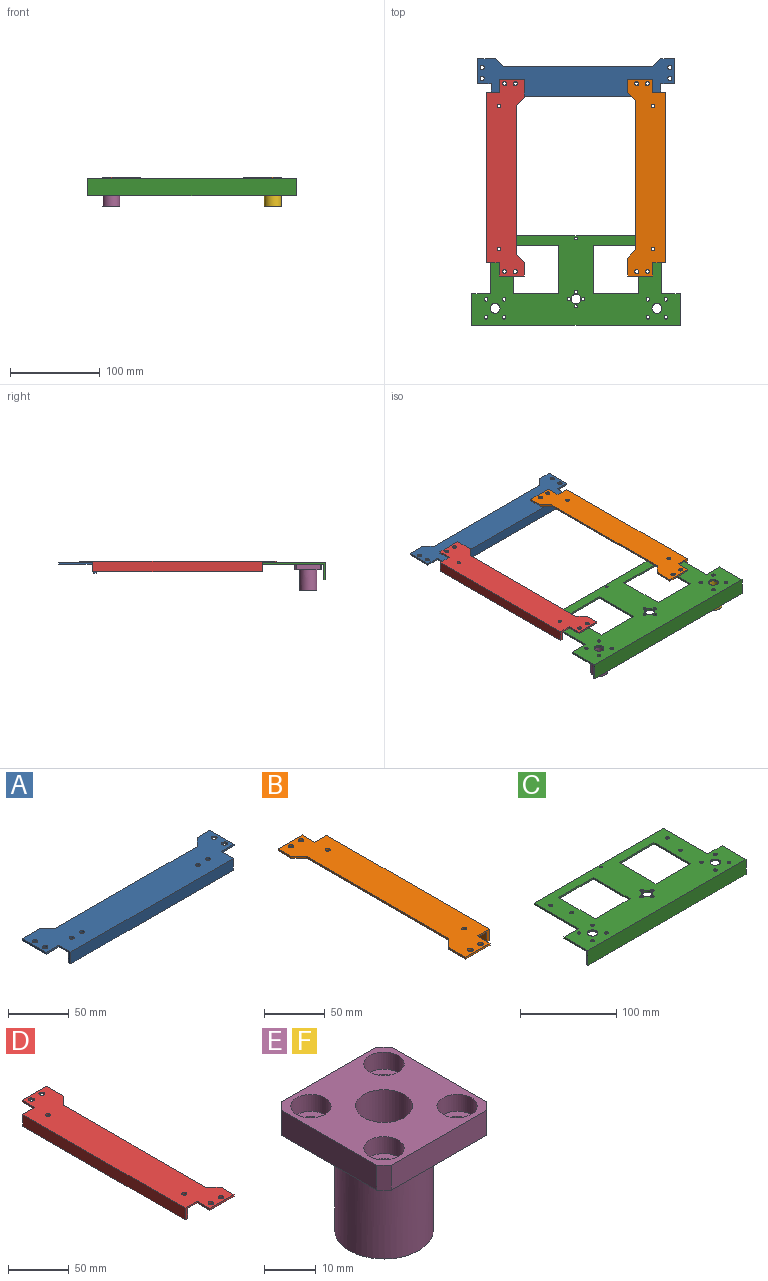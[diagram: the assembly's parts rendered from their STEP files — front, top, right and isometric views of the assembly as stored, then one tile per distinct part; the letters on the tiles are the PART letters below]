
ASSEMBLY  parts=6 mates=5
PART A: 24 faces, bbox 219x42x11.8 mm
  f0: plane 219x39mm, normal (0,0,-1), area 6519.3mm2, adj f2,f3,f4,f5,f6,f7,f8,f9
  f1: plane 219x42mm, normal (0,0,1), area 7086.3mm2, adj f2,f3,f4,f5,f6,f7,f8,f9
  f2: plane 14x11.8mm, normal (1,0,0), area 55.2mm2, adj f0,f1,f3,f18,f20,f21
  f3: plane 15x1.8mm, normal (0,-1,0), area 27mm2, adj f0,f1,f2,f4
  f4: plane 28x1.8mm, normal (1,0,0), area 50.4mm2, adj f0,f1,f3,f5
  f5: plane 15x1.8mm, normal (0,1,0), area 27mm2, adj f0,f1,f4,f6
  f6: plane 9x9mm, normal (-0.71,0.71,0), area 22.9mm2, adj f0,f1,f5,f7
  f7: plane 166x1.8mm, normal (0,1,0), area 298.8mm2, adj f0,f1,f6,f8
  f8: plane 9x9mm, normal (0.71,0.71,0), area 22.9mm2, adj f0,f1,f7,f9
  f9: plane 20x1.8mm, normal (0,1,0), area 36mm2, adj f0,f1,f8,f10
  f10: plane 28x1.8mm, normal (-1,0,0), area 50.4mm2, adj f0,f1,f9,f11
  f11: plane 15x1.8mm, normal (0,-1,0), area 27mm2, adj f0,f1,f10,f12
  f12: plane 14x11.8mm, normal (-1,0,0), area 55.2mm2, adj f0,f1,f11,f18,f20,f21
  f13: cylinder r=2.3mm len=4.6mm, axis (0,0,-1), area 26mm2, adj f0,f1
  f14: cylinder r=2.3mm len=4.6mm, axis (0,0,-1), area 26mm2, adj f0,f1
  f15: cylinder r=2.3mm len=4.6mm, axis (0,0,-1), area 26mm2, adj f0,f1
  f16: cylinder r=2.3mm len=4.6mm, axis (0,0,-1), area 26mm2, adj f0,f1
  f17: cylinder r=2mm len=4mm, axis (0,0,-1), area 22.6mm2, adj f0,f1
  f18: plane 189x11.8mm, normal (0,-1,0), area 2230.2mm2, adj f1,f2,f12,f21
  f19: cylinder r=2mm len=4mm, axis (0,0,-1), area 22.6mm2, adj f0,f1
  f20: plane 189x10mm, normal (0,1,0), area 1890mm2, adj f0,f2,f12,f21
  f21: plane 189x3mm, normal (0,0,-1), area 567mm2, adj f2,f12,f18,f20
  f22: cylinder r=2mm len=4mm, axis (0,0,-1), area 22.6mm2, adj f0,f1
  f23: cylinder r=2mm len=4mm, axis (0,0,-1), area 22.6mm2, adj f0,f1
PART B: 22 faces, bbox 42x219x11.8 mm
  f0: plane 219x39mm, normal (0,0,-1), area 6544.4mm2, adj f1,f2,f3,f4,f5,f6,f7,f8
  f1: plane 14x11.8mm, normal (0,1,0), area 55.2mm2, adj f0,f2,f17,f19,f20,f21
  f2: plane 15x1.8mm, normal (1,0,0), area 27mm2, adj f0,f1,f3,f19
  f3: plane 28x1.8mm, normal (0,1,0), area 50.4mm2, adj f0,f2,f4,f19
  f4: plane 15x1.8mm, normal (-1,0,0), area 27mm2, adj f0,f3,f5,f19
  f5: plane 9x9mm, normal (-0.71,-0.71,0), area 22.9mm2, adj f0,f4,f6,f19
  f6: plane 166x1.8mm, normal (-1,0,0), area 298.8mm2, adj f0,f5,f7,f19
  f7: plane 9x9mm, normal (-0.71,0.71,0), area 22.9mm2, adj f0,f6,f8,f19
  f8: plane 20x1.8mm, normal (-1,0,0), area 36mm2, adj f0,f7,f9,f19
  f9: plane 28x1.8mm, normal (0,-1,0), area 50.4mm2, adj f0,f8,f10,f19
  f10: plane 15x1.8mm, normal (1,0,0), area 27mm2, adj f0,f9,f11,f19
  f11: plane 14x11.8mm, normal (0,-1,0), area 55.2mm2, adj f0,f10,f17,f19,f20,f21
  f12: cylinder r=2.3mm len=4.6mm, axis (0,0,-1), area 26mm2, adj f0,f19
  f13: cylinder r=2.3mm len=4.6mm, axis (0,0,-1), area 26mm2, adj f0,f19
  f14: cylinder r=2.3mm len=4.6mm, axis (0,0,-1), area 26mm2, adj f0,f19
  f15: cylinder r=2.3mm len=4.6mm, axis (0,0,-1), area 26mm2, adj f0,f19
  f16: cylinder r=2mm len=4mm, axis (0,0,-1), area 22.6mm2, adj f0,f19
  f17: plane 189x11.8mm, normal (1,0,0), area 2230.2mm2, adj f1,f11,f19,f21
  f18: cylinder r=2mm len=4mm, axis (0,0,-1), area 22.6mm2, adj f0,f19
  f19: plane 219x42mm, normal (0,0,1), area 7111.4mm2, adj f1,f2,f3,f4,f5,f6,f7,f8
  f20: plane 189x10mm, normal (-1,0,0), area 1890mm2, adj f0,f1,f11,f21
  f21: plane 189x3mm, normal (0,0,-1), area 567mm2, adj f1,f11,f17,f20
PART C: 40 faces, bbox 232x100x19 mm
  f0: plane 232x98mm, normal (0,0,-1), area 14016.6mm2, adj f1,f2,f3,f4,f5,f6,f7,f8
  f1: plane 54x2mm, normal (1,0,0), area 108mm2, adj f0,f2,f23,f37
  f2: plane 51x2mm, normal (0,-1,0), area 102mm2, adj f0,f1,f3,f37
  f3: plane 54x2mm, normal (-1,0,0), area 108mm2, adj f0,f2,f23,f37
  f4: plane 51x2mm, normal (0,1,0), area 102mm2, adj f0,f5,f24,f37
  f5: plane 54x2mm, normal (1,0,0), area 108mm2, adj f0,f4,f6,f37
  f6: plane 51x2mm, normal (0,-1,0), area 102mm2, adj f0,f5,f24,f37
  f7: plane 35x19mm, normal (1,0,0), area 104mm2, adj f0,f8,f35,f37,f38,f39
  f8: plane 21x2mm, normal (0,1,0), area 42mm2, adj f0,f7,f9,f37
  f9: plane 65x2mm, normal (1,0,0), area 130mm2, adj f0,f8,f10,f37
  f10: plane 190x2mm, normal (0,1,0), area 380mm2, adj f0,f9,f11,f37
  f11: plane 65x2mm, normal (-1,0,0), area 130mm2, adj f0,f10,f12,f37
  f12: plane 21x2mm, normal (0,1,0), area 42mm2, adj f0,f11,f13,f37
  f13: plane 35x19mm, normal (-1,0,0), area 104mm2, adj f0,f12,f35,f37,f38,f39
  f14: cylinder r=2mm len=4mm, axis (0,0,-1), area 25.1mm2, adj f0,f37
  f15: cylinder r=2mm len=4mm, axis (0,0,-1), area 25.1mm2, adj f0,f37
  f16: cylinder r=5.5mm len=11mm, axis (0,0,-1), area 69.1mm2, adj f0,f37
  f17: cylinder r=5.5mm len=11mm, axis (0,0,-1), area 69.1mm2, adj f0,f37
  f18: cylinder r=1.75mm len=3.5mm, axis (0,0,-1), area 22mm2, adj f0,f37
  f19: cylinder r=1.75mm len=3.5mm, axis (0,0,-1), area 22mm2, adj f0,f37
  f20: cylinder r=1.75mm len=3.5mm, axis (0,0,-1), area 22mm2, adj f0,f37
  f21: cylinder r=1.75mm len=3.5mm, axis (0,0,-1), area 22mm2, adj f0,f37
  f22: cylinder r=5.5mm len=11mm, axis (0,0,-1), area 69.1mm2, adj f0,f37
  f23: plane 51x2mm, normal (0,1,0), area 102mm2, adj f0,f1,f3,f37
  f24: plane 54x2mm, normal (-1,0,0), area 108mm2, adj f0,f4,f6,f37
  f25: cylinder r=2mm len=4mm, axis (0,0,-1), area 25.1mm2, adj f0,f37
  f26: cylinder r=2mm len=4mm, axis (0,0,-1), area 25.1mm2, adj f0,f37
  f27: cylinder r=2mm len=4mm, axis (0,0,-1), area 25.1mm2, adj f0,f37
  f28: cylinder r=2mm len=4mm, axis (0,0,-1), area 25.1mm2, adj f0,f37
  f29: cylinder r=2mm len=4mm, axis (0,0,-1), area 25.1mm2, adj f0,f37
  f30: cylinder r=2mm len=4mm, axis (0,0,-1), area 25.1mm2, adj f0,f37
  f31: cylinder r=1.5mm len=3mm, axis (0,0,-1), area 18.8mm2, adj f0,f37
  f32: cylinder r=2mm len=4mm, axis (0,0,-1), area 25.1mm2, adj f0,f37
  f33: cylinder r=2mm len=4mm, axis (0,0,-1), area 25.1mm2, adj f0,f37
  f34: cylinder r=2mm len=4mm, axis (0,0,-1), area 25.1mm2, adj f0,f37
  f35: plane 232x19mm, normal (0,-1,0), area 4408mm2, adj f7,f13,f37,f39
  f36: cylinder r=2mm len=4mm, axis (0,0,-1), area 25.1mm2, adj f0,f37
  f37: plane 232x100mm, normal (0,0,1), area 14480.6mm2, adj f1,f2,f3,f4,f5,f6,f7,f8
  f38: plane 232x17mm, normal (0,1,0), area 3944mm2, adj f0,f7,f13,f39
  f39: plane 232x2mm, normal (0,0,-1), area 464mm2, adj f7,f13,f35,f38
PART D: 22 faces, bbox 42x219x11.8 mm
  f0: plane 219x39mm, normal (0,0,-1), area 6544.4mm2, adj f1,f2,f3,f4,f5,f6,f7,f8
  f1: plane 14x11.8mm, normal (0,-1,0), area 55.2mm2, adj f0,f2,f17,f19,f20,f21
  f2: plane 15x1.8mm, normal (-1,0,0), area 27mm2, adj f0,f1,f3,f19
  f3: plane 28x1.8mm, normal (0,-1,0), area 50.4mm2, adj f0,f2,f4,f19
  f4: plane 15x1.8mm, normal (1,0,0), area 27mm2, adj f0,f3,f5,f19
  f5: plane 9x9mm, normal (0.71,0.71,0), area 22.9mm2, adj f0,f4,f6,f19
  f6: plane 166x1.8mm, normal (1,0,0), area 298.8mm2, adj f0,f5,f7,f19
  f7: plane 9x9mm, normal (0.71,-0.71,0), area 22.9mm2, adj f0,f6,f8,f19
  f8: plane 20x1.8mm, normal (1,0,0), area 36mm2, adj f0,f7,f9,f19
  f9: plane 28x1.8mm, normal (0,1,0), area 50.4mm2, adj f0,f8,f10,f19
  f10: plane 15x1.8mm, normal (-1,0,0), area 27mm2, adj f0,f9,f11,f19
  f11: plane 14x11.8mm, normal (0,1,0), area 55.2mm2, adj f0,f10,f17,f19,f20,f21
  f12: cylinder r=2.3mm len=4.6mm, axis (0,0,-1), area 26mm2, adj f0,f19
  f13: cylinder r=2.3mm len=4.6mm, axis (0,0,-1), area 26mm2, adj f0,f19
  f14: cylinder r=2.3mm len=4.6mm, axis (0,0,-1), area 26mm2, adj f0,f19
  f15: cylinder r=2.3mm len=4.6mm, axis (0,0,-1), area 26mm2, adj f0,f19
  f16: cylinder r=2mm len=4mm, axis (0,0,-1), area 22.6mm2, adj f0,f19
  f17: plane 189x11.8mm, normal (-1,0,0), area 2230.2mm2, adj f1,f11,f19,f21
  f18: cylinder r=2mm len=4mm, axis (0,0,-1), area 22.6mm2, adj f0,f19
  f19: plane 219x42mm, normal (0,0,1), area 7111.4mm2, adj f1,f2,f3,f4,f5,f6,f7,f8
  f20: plane 189x10mm, normal (1,0,0), area 1890mm2, adj f0,f1,f11,f21
  f21: plane 189x3mm, normal (0,0,-1), area 567mm2, adj f1,f11,f17,f20
PART E: 25 faces, bbox 30x30x29.5 mm
  f0: plane 26x5.9mm, normal (0,1,0), area 153.4mm2, adj f9,f10,f21,f22
  f1: plane 26x5.9mm, normal (1,0,0), area 153.4mm2, adj f9,f10,f22,f23
  f2: plane 26x5.9mm, normal (0,-1,0), area 153.4mm2, adj f9,f10,f23,f24
  f3: cylinder r=2.25mm len=4.5mm, axis (0,0,1), area 26.9mm2, adj f9,f16
  f4: cylinder r=2.25mm len=4.5mm, axis (0,0,1), area 26.9mm2, adj f9,f14
  f5: cylinder r=5.5mm len=29.5mm, axis (0,0,1), area 1019.4mm2, adj f10,f12
  f6: cylinder r=2.25mm len=4.5mm, axis (0,0,1), area 26.9mm2, adj f9,f20
  f7: plane 26x5.9mm, normal (-1,0,0), area 153.4mm2, adj f9,f10,f21,f24
  f8: cylinder r=2.25mm len=4.5mm, axis (0,0,1), area 26.9mm2, adj f9,f18
  f9: plane 30x30mm, normal (0,0,-1), area 544.9mm2, adj f0,f1,f2,f3,f4,f6,f7,f8
  f10: plane 30x30mm, normal (0,0,1), area 605.8mm2, adj f0,f1,f2,f5,f7,f13,f15,f17
  f11: cylinder r=9.5mm len=23.6mm, axis (0,0,1), area 1408.7mm2, adj f9,f12
  f12: plane 19x19mm, normal (0,0,-1), area 188.5mm2, adj f5,f11
  f13: cylinder r=3.9mm len=7.8mm, axis (0,0,1), area 98mm2, adj f10,f14
  f14: plane 7.8x7.8mm, normal (0,0,1), area 31.9mm2, adj f4,f13
  f15: cylinder r=3.9mm len=7.8mm, axis (0,0,1), area 98mm2, adj f10,f16
  f16: plane 7.8x7.8mm, normal (0,0,1), area 31.9mm2, adj f3,f15
  f17: cylinder r=3.9mm len=7.8mm, axis (0,0,1), area 98mm2, adj f10,f18
  f18: plane 7.8x7.8mm, normal (0,0,1), area 31.9mm2, adj f8,f17
  f19: cylinder r=3.9mm len=7.8mm, axis (0,0,1), area 98mm2, adj f10,f20
  f20: plane 7.8x7.8mm, normal (0,0,1), area 31.9mm2, adj f6,f19
  f21: plane 5.9x2mm, normal (-0.71,0.71,0), area 16.7mm2, adj f0,f7,f9,f10
  f22: plane 5.9x2mm, normal (0.71,0.71,0), area 16.7mm2, adj f0,f1,f9,f10
  f23: plane 5.9x2mm, normal (0.71,-0.71,0), area 16.7mm2, adj f1,f2,f9,f10
  f24: plane 5.9x2mm, normal (-0.71,-0.71,0), area 16.7mm2, adj f2,f7,f9,f10
PART F: same geometry as E
PLACE A t=(0,0,0.2)mm
PLACE B at identity
PLACE C at identity fixed
PLACE D at identity
PLACE E t=(-180,0,0)mm
PLACE F at identity
MATE fastened F.f6 <-> C.f28  axis (0,0,1) through (100,9,0)mm
MATE fastened B.f12 <-> C.f32  axis (0,0,-1) through (79.5,60,2)mm
MATE fastened C.f36 <-> D.f13  axis (0,0,1) through (-79.5,60,2)mm
MATE fastened D.f15 <-> A.f23  axis (0,0,-1) through (-67.5,269,2)mm
MATE fastened E.f6 <-> C.f14  axis (0,0,1) through (-80,9,0)mm
